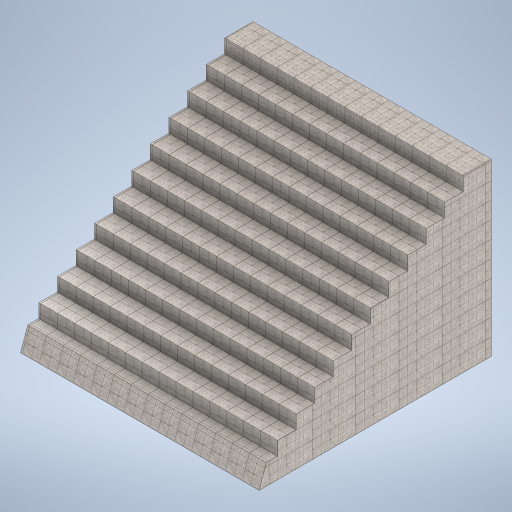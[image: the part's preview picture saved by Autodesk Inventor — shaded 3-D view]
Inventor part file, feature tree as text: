
AUTODESK INVENTOR PART (.ipt)
format: ipt  version: 2024.2 (Build 282272000, 272)  size: 555,008 bytes
history: native  units: mm
features: extrude x3, sketch x3
ambient origin geometry x8: Origin, YZ Plane, XZ Plane, XY Plane, X Axis, Y Axis, Z Axis, Center Point
bodies: Solid1 (feature_tree)
feature tree (6):
  extrude  "Extrusion1"  Depth=2000.0mm
  extrude  "Extrusion2"  Depth=2000.0mm
  extrude  "Extrusion3"  Depth=2800.0mm TaperAngle=0.0deg
  sketch  "Sketch1"  dims[d0=2800.0mm d1=2000.0mm]
  sketch  "Sketch2"  dims[d2=2000.0mm d3=0.0mm d4=19.198622mm]
  sketch  "Sketch3"  dims[d5=2800.0mm d6=0.0mm d7=160.0mm d8=160.0mm d9=160.0mm d10=160.0mm d11=160.0mm d12=160.0mm d13=160.0mm d14=160.0mm d15=160.0mm d16=160.0mm d17=160.0mm d18=160.0mm d19=218.0mm d20=218.0mm d21=218.0mm d22=218.0mm d23=218.0mm d24=218.0mm d25=218.0mm d26=218.0mm d27=218.0mm d28=218.0mm d29=218.0mm d30=218.0mm d31=2800.0mm d32=0.0mm]
